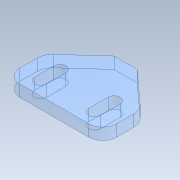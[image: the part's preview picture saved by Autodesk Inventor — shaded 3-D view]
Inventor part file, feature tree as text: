
AUTODESK INVENTOR PART (.ipt)
format: ipt  version: 2022 (Build 260153000, 153)  size: 185,344 bytes
history: native  units: mm
features: sketch x2, extrude x1
ambient origin geometry x8: Origin, YZ Plane, XZ Plane, XY Plane, X Axis, Y Axis, Z Axis, Center Point
bodies: Solid1 (feature_tree)
feature tree (3):
  sketch  "3D Sketch1"
  extrude  "Extrusion1"  [1 undecoded]
  sketch  "Sketch8"  dims[d1=3.0mm d2=0.0mm]
note: 1 required parameter value undecoded (feature->parameter linkage not recoverable at this tier; creation-order binding heuristic only, values carry confidence <= 0.55)
